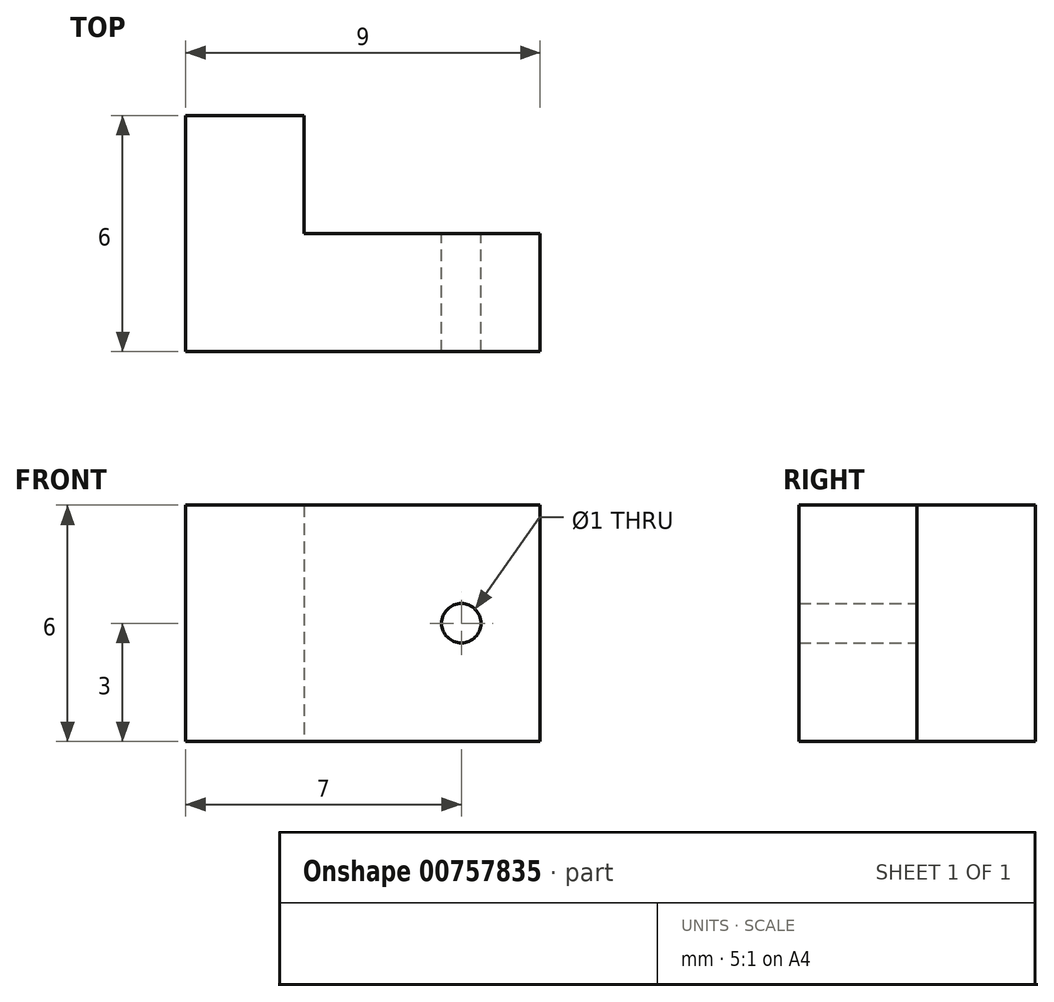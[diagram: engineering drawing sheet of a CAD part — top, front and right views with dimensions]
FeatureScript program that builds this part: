
annotation { "Feature Type Name" : "Feature", "Feature Type Description" : "" }
export const myFeature = defineFeature(function(context is Context, id is Id, definition is map)
    precondition{}
    {
        {
            var Q0;
            Q0=qCreatedBy(makeId("Top.planeOp"),FACE);
            var sketch = newSketch(context, id + "F0", { "sketchPlane" : qUnion([Q0])});
            skLineSegment(sketch, "E0", {"start": v(0, 0) * mm, "end": v(9, 0) * mm});
            skLineSegment(sketch, "E1", {"start": v(9, 0) * mm, "end": v(9, 3) * mm});
            skLineSegment(sketch, "E2", {"start": v(9, 3) * mm, "end": v(3, 3) * mm});
            skLineSegment(sketch, "E3", {"start": v(3, 3) * mm, "end": v(3, 6) * mm});
            skLineSegment(sketch, "E4", {"start": v(3, 6) * mm, "end": v(0, 6) * mm});
            skLineSegment(sketch, "E5", {"start": v(0, 6) * mm, "end": v(0, 0) * mm});
            skSolve(sketch);
        }
        {
            var Q0;
            Q0 = qSketchRegion(id + "F0", true);
            extrude(context, id + "F1", {"entities" : qUnion([Q0]), "depth" : 6 * mm, "offsetDistance" : 25 * mm});
        }
        {
            var Q0;
            Q0=makeQuery(id+"F1.opExtrude","SWEPT_FACE",FACE,{"disambiguationData":[OSD([sQuery(id+"F0.wireOp",EDGE,"E2")])]});
            var sketch = newSketch(context, id + "F2", { "sketchPlane" : qUnion([Q0])});
            skCircle(sketch, "E6", {"center": v(-7, 3) * mm, "radius": 0.5 * mm});
            skSolve(sketch);
        }
        {
            var Q0;
            Q0 = qSketchRegion(id + "F2", true);
            extrude(context, id + "F3", {"entities" : qUnion([Q0]), "operationType" : NewBodyOperationType.REMOVE, "endBound" : BoundingType.THROUGH_ALL, "oppositeDirection" : true, "depth" : 25 * mm, "offsetDistance" : 25 * mm});
        }
    });
